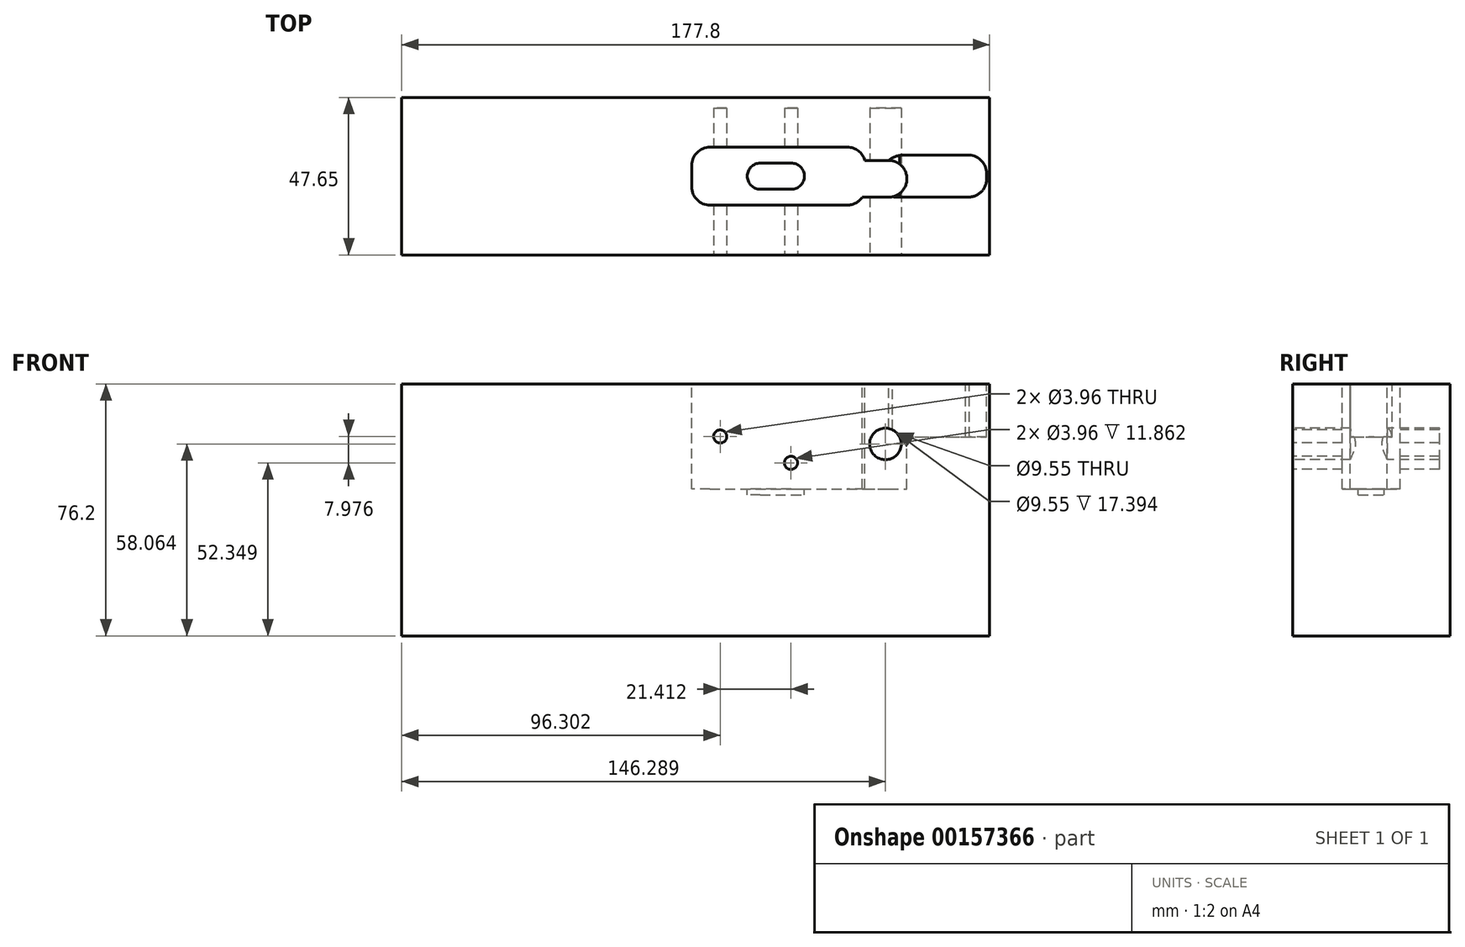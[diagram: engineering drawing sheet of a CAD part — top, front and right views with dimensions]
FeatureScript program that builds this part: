
annotation { "Feature Type Name" : "Feature", "Feature Type Description" : "" }
export const myFeature = defineFeature(function(context is Context, id is Id, definition is map)
    precondition{}
    {
        {
            var Q0;
            Q0=qCreatedBy(makeId("Top.planeOp"),FACE);
            var sketch = newSketch(context, id + "F0", { "sketchPlane" : qUnion([Q0])});
            skLineSegment(sketch, "E0.bottom", {"start": v(-4.76, 42.89) * mm, "end": v(173.04, 42.89) * mm});
            skLineSegment(sketch, "E0.top", {"start": v(-4.76, -4.76) * mm, "end": v(173.04, -4.76) * mm});
            skLineSegment(sketch, "E0.left", {"start": v(-4.76, 42.89) * mm, "end": v(-4.76, -4.76) * mm});
            skLineSegment(sketch, "E0.right", {"start": v(173.04, 42.89) * mm, "end": v(173.04, -4.76) * mm});
            skLineSegment(sketch, "E1", {"start": v(194, 19.06) * mm, "end": v(-68.25, 19.06) * mm, "construction": true});
            skPoint(sketch, "E1.startSnap0", {"position": v(173.04, 19.06) * mm});
            skPoint(sketch, "E1.endSnap0", {"position": v(-4.76, 19.06) * mm});
            skSolve(sketch);
        }
        {
            var Q0;
            Q0=makeQuery(id+"F0.imprint","IMPRINT",FACE,{"disambiguationData":[TD([[makeQuery(id+"F0.imprint","IMPRINT",EDGE,{"derivedFrom":sQuery(id+"F0.wireOp",EDGE,"229dbb7b-168f-4076-88b1-1792d4879c7d.bottom")}),-1.0]])]});
            var Q1;
            Q1=makeQuery(id+"F0.imprint","IMPRINT",FACE,{"disambiguationData":[TD([[makeQuery(id+"F0.imprint","IMPRINT",EDGE,{"derivedFrom":sQuery(id+"F0.wireOp",EDGE,"E0.bottom")}),-1.0]])]});
            extrude(context, id + "F1", {"entities" : qUnion([Q0, Q1]), "oppositeDirection" : true, "depth" : 76.2 * mm});
        }
        {
            var Q0;
            Q0=makeQuery(id+"F1.opExtrude","SWEPT_FACE",FACE,{"disambiguationData":[OSD([sQuery(id+"F0.wireOp",EDGE,"E0.top")])]});
            var sketch = newSketch(context, id + "F2", { "sketchPlane" : qUnion([Q0])});
            skCircle(sketch, "E2", {"center": v(161.93, -6.35) * mm, "radius": 3.18 * mm, "construction": true});
            skCircle(sketch, "E3", {"center": v(0, -6.35) * mm, "radius": 3.18 * mm, "construction": true});
            skCircle(sketch, "E4", {"center": v(141.53, -18.14) * mm, "radius": 4.78 * mm});
            skCircle(sketch, "E5", {"center": v(112.95, -23.85) * mm, "radius": 1.98 * mm});
            skCircle(sketch, "E6", {"center": v(91.54, -15.87) * mm, "radius": 1.98 * mm});
            skPoint(sketch, "E7", {"position": v(-4.76, -76.2) * mm});
            skLineSegment(sketch, "E8", {"start": v(0, 1.12) * mm, "end": v(0, -22.4) * mm});
            skSolve(sketch);
        }
        {
            var Q0;
            Q0=qSketchRegion(id+"F2",true);
            extrude(context, id + "F3", {"entities" : qUnion([Q0]), "operationType" : NewBodyOperationType.REMOVE, "oppositeDirection" : true, "depth" : 44.45 * mm});
        }
        {
            var Q0;
            Q0=makeQuery(id+"F0.imprint","IMPRINT",FACE,{"disambiguationData":[TD([[makeQuery(id+"F0.imprint","IMPRINT",EDGE,{"derivedFrom":sQuery(id+"F0.wireOp",EDGE,"E0.bottom")}),-1.0]])]});
            var sketch = newSketch(context, id + "F4", { "sketchPlane" : qUnion([Q0])});
            skLineSegment(sketch, "E9.right", {"start": v(172.14, 19.9) * mm, "end": v(172.14, 18.27) * mm});
            skPoint(sketch, "E10.visualSharp", {"position": v(172.14, 25.43) * mm});
            skArc(sketch, "E10.filletArc", {"start": v(172.14, 19.9) * mm, "mid": v(170.61, 23.71) * mm, "end": v(166.89, 25.43) * mm});
            skPoint(sketch, "E11.visualSharp", {"position": v(172.14, 12.73) * mm});
            skArc(sketch, "E11.filletArc", {"start": v(165.79, 12.79) * mm, "mid": v(170.22, 14.07) * mm, "end": v(172.14, 18.27) * mm});
            skPoint(sketch, "E12.visualSharp", {"position": v(142.53, 46.05) * mm});
            skLineSegment(sketch, "E13", {"start": v(147.12, 25.43) * mm, "end": v(166.89, 25.43) * mm});
            skLineSegment(sketch, "E14", {"start": v(0, 63.67) * mm, "end": v(0, -4.76) * mm, "construction": true});
            skLineSegment(sketch, "E15", {"start": v(145.03, 25.41) * mm, "end": v(145.03, 25.41) * mm});
            skLineSegment(sketch, "E16", {"start": v(139.5, 17.8) * mm, "end": v(139.5, 17.55) * mm});
            skLineSegment(sketch, "E17", {"start": v(144.26, 12.79) * mm, "end": v(165.79, 12.79) * mm});
            skPoint(sketch, "E18.visualSharp", {"position": v(139.5, 25.41) * mm});
            skPoint(sketch, "E19.visualSharp", {"position": v(139.5, 12.79) * mm});
            skArc(sketch, "E19.filletArc", {"start": v(139.5, 17.55) * mm, "mid": v(140.9, 14.18) * mm, "end": v(144.26, 12.79) * mm});
            skPoint(sketch, "E20.newPointA", {"position": v(149.26, 25.43) * mm});
            skArc(sketch, "E20.filletArc", {"start": v(147.12, 25.43) * mm, "mid": v(141.73, 23.2) * mm, "end": v(139.5, 17.8) * mm});
            skSolve(sketch);
        }
        {
            var Q0;
            Q0=qSketchRegion(id+"F4",true);
            extrude(context, id + "F5", {"entities" : qUnion([Q0]), "operationType" : NewBodyOperationType.REMOVE, "oppositeDirection" : true, "depth" : 16 * mm});
        }
        {
            var Q0;
            Q0=makeQuery(id+"F0.imprint","IMPRINT",FACE,{"disambiguationData":[TD([[makeQuery(id+"F0.imprint","IMPRINT",EDGE,{"derivedFrom":sQuery(id+"F0.wireOp",EDGE,"E0.bottom")}),-1.0]])]});
            var sketch = newSketch(context, id + "F6", { "sketchPlane" : qUnion([Q0])});
            skLineSegment(sketch, "E21.bottom", {"start": v(103.7, 23.03) * mm, "end": v(113.06, 23.03) * mm});
            skLineSegment(sketch, "E21.top", {"start": v(103.7, 15.1) * mm, "end": v(113.06, 15.1) * mm});
            skLineSegment(sketch, "E21.left", {"start": v(99.75, 19.07) * mm, "end": v(99.75, 19.07) * mm});
            skLineSegment(sketch, "E21.right", {"start": v(117.02, 19.07) * mm, "end": v(117.02, 19.07) * mm});
            skPoint(sketch, "E22.visualSharp", {"position": v(99.75, 23.03) * mm});
            skArc(sketch, "E22.filletArc", {"start": v(103.7, 23.03) * mm, "mid": v(100.9, 21.87) * mm, "end": v(99.75, 19.07) * mm});
            skPoint(sketch, "E23.visualSharp", {"position": v(117.02, 23.03) * mm});
            skArc(sketch, "E23.filletArc", {"start": v(117.02, 19.07) * mm, "mid": v(115.86, 21.87) * mm, "end": v(113.06, 23.03) * mm});
            skPoint(sketch, "E24.visualSharp", {"position": v(117.02, 15.1) * mm});
            skArc(sketch, "E24.filletArc", {"start": v(113.06, 15.1) * mm, "mid": v(115.86, 16.27) * mm, "end": v(117.02, 19.07) * mm});
            skPoint(sketch, "E25.visualSharp", {"position": v(99.75, 15.1) * mm});
            skArc(sketch, "E25.filletArc", {"start": v(99.75, 19.07) * mm, "mid": v(100.9, 16.27) * mm, "end": v(103.7, 15.1) * mm});
            skSolve(sketch);
        }
        {
            var Q0;
            Q0=qSketchRegion(id+"F6",true);
            extrude(context, id + "F7", {"entities" : qUnion([Q0]), "operationType" : NewBodyOperationType.REMOVE, "oppositeDirection" : true, "depth" : 33.53 * mm});
        }
        {
            var Q0;
            Q0=makeQuery(id+"F0.imprint","IMPRINT",FACE,{"disambiguationData":[TD([[makeQuery(id+"F0.imprint","IMPRINT",EDGE,{"derivedFrom":sQuery(id+"F0.wireOp",EDGE,"E0.bottom")}),-1.0]])]});
            var sketch = newSketch(context, id + "F8", { "sketchPlane" : qUnion([Q0])});
            skLineSegment(sketch, "E26.bottom", {"start": v(88.47, 27.83) * mm, "end": v(130, 27.83) * mm});
            skLineSegment(sketch, "E26.top", {"start": v(88.47, 10.3) * mm, "end": v(130, 10.3) * mm});
            skLineSegment(sketch, "E26.left", {"start": v(82.93, 22.29) * mm, "end": v(82.93, 15.84) * mm});
            skLineSegment(sketch, "E26.right", {"start": v(135.53, 22.29) * mm, "end": v(135.53, 15.84) * mm});
            skLineSegment(sketch, "E27.left", {"start": v(152.8, 51.59) * mm, "end": v(152.8, 51.64) * mm});
            skLineSegment(sketch, "E27.right", {"start": v(129.37, 51.59) * mm, "end": v(129.37, 51.64) * mm});
            skPoint(sketch, "E28.visualSharp", {"position": v(135.53, 27.83) * mm});
            skArc(sketch, "E28.filletArc", {"start": v(135.53, 22.29) * mm, "mid": v(133.91, 26.2) * mm, "end": v(130, 27.83) * mm});
            skPoint(sketch, "E29.visualSharp", {"position": v(135.53, 10.3) * mm});
            skArc(sketch, "E29.filletArc", {"start": v(130, 10.3) * mm, "mid": v(133.91, 11.92) * mm, "end": v(135.53, 15.84) * mm});
            skPoint(sketch, "E30.visualSharp", {"position": v(82.93, 27.83) * mm});
            skArc(sketch, "E30.filletArc", {"start": v(88.47, 27.83) * mm, "mid": v(84.55, 26.2) * mm, "end": v(82.93, 22.29) * mm});
            skPoint(sketch, "E31.visualSharp", {"position": v(82.93, 10.3) * mm});
            skArc(sketch, "E31.filletArc", {"start": v(82.93, 15.84) * mm, "mid": v(84.55, 11.92) * mm, "end": v(88.47, 10.3) * mm});
            skSolve(sketch);
        }
        {
            var Q0;
            Q0=qSketchRegion(id+"F8",true);
            extrude(context, id + "F9", {"entities" : qUnion([Q0]), "operationType" : NewBodyOperationType.REMOVE, "oppositeDirection" : true, "depth" : 31.72 * mm});
        }
        {
            var Q0;
            Q0=makeQuery(id+"F8.imprint","IMPRINT",FACE,{"disambiguationData":[TD([[makeQuery(id+"F8.imprint","IMPRINT",EDGE,{"derivedFrom":sQuery(id+"F8.wireOp",EDGE,"E26.bottom")}),1.0]])]});
            var sketch = newSketch(context, id + "F10", { "sketchPlane" : qUnion([Q0])});
            skLineSegment(sketch, "E32.bottom", {"start": v(134.52, 23.84) * mm, "end": v(142.47, 23.84) * mm});
            skLineSegment(sketch, "E32.top", {"start": v(134.52, 12.71) * mm, "end": v(142.47, 12.71) * mm});
            skLineSegment(sketch, "E32.left", {"start": v(131.35, 20.66) * mm, "end": v(131.35, 15.89) * mm});
            skLineSegment(sketch, "E32.right", {"start": v(148, 18.3) * mm, "end": v(148, 18.25) * mm});
            skPoint(sketch, "E33.visualSharp", {"position": v(148, 23.84) * mm});
            skArc(sketch, "E33.filletArc", {"start": v(148, 18.3) * mm, "mid": v(146.38, 22.22) * mm, "end": v(142.47, 23.84) * mm});
            skPoint(sketch, "E34.visualSharp", {"position": v(148, 12.71) * mm});
            skArc(sketch, "E34.filletArc", {"start": v(142.47, 12.71) * mm, "mid": v(146.38, 14.33) * mm, "end": v(148, 18.25) * mm});
            skPoint(sketch, "E35.visualSharp", {"position": v(131.35, 23.84) * mm});
            skArc(sketch, "E35.filletArc", {"start": v(134.52, 23.84) * mm, "mid": v(132.28, 22.9) * mm, "end": v(131.35, 20.66) * mm});
            skPoint(sketch, "E36.visualSharp", {"position": v(131.35, 12.71) * mm});
            skArc(sketch, "E36.filletArc", {"start": v(131.35, 15.89) * mm, "mid": v(132.28, 13.64) * mm, "end": v(134.52, 12.71) * mm});
            skSolve(sketch);
        }
        {
            var Q0;
            Q0=qSketchRegion(id+"F10",true);
            extrude(context, id + "F11", {"entities" : qUnion([Q0]), "operationType" : NewBodyOperationType.REMOVE, "oppositeDirection" : true, "depth" : 31.72 * mm});
        }
    });
